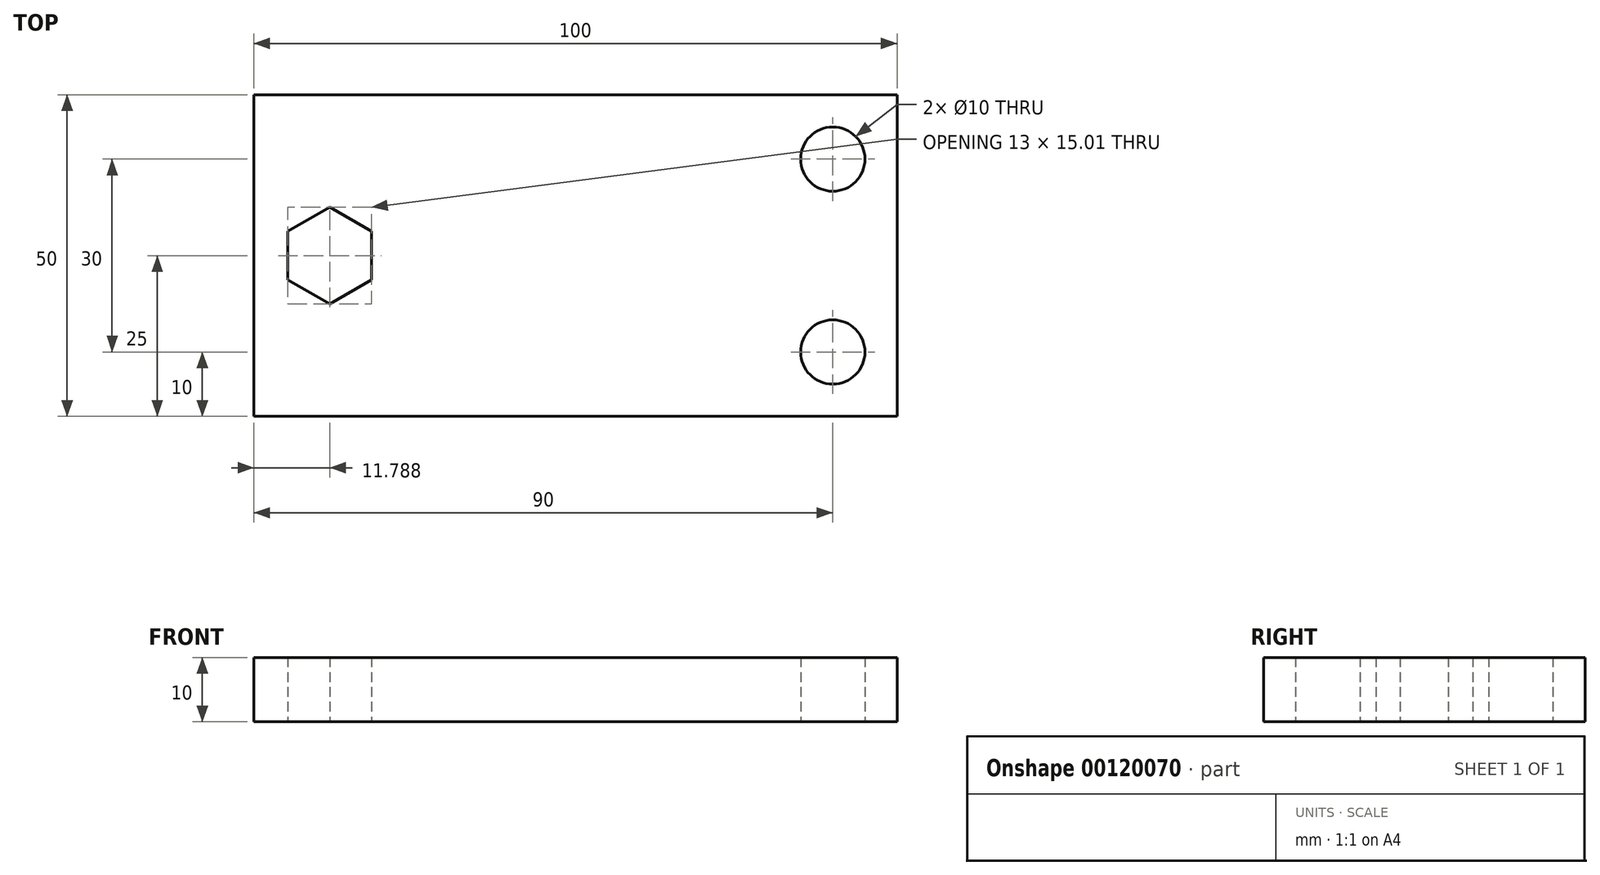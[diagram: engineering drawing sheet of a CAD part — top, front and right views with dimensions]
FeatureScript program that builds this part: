
annotation { "Feature Type Name" : "Feature", "Feature Type Description" : "" }
export const myFeature = defineFeature(function(context is Context, id is Id, definition is map)
    precondition{}
    {
        {
            var Q0;
            Q0=qCreatedBy(makeId("Top.planeOp"),FACE);
            var sketch = newSketch(context, id + "F0", { "sketchPlane" : qUnion([Q0])});
            skLineSegment(sketch, "E0.bottom", {"start": v(50, -25) * mm, "end": v(-50, -25) * mm});
            skLineSegment(sketch, "E0.top", {"start": v(50, 25) * mm, "end": v(-50, 25) * mm});
            skLineSegment(sketch, "E0.left", {"start": v(50, -25) * mm, "end": v(50, 25) * mm});
            skLineSegment(sketch, "E0.right", {"start": v(-50, -25) * mm, "end": v(-50, 25) * mm});
            skPoint(sketch, "E0.middle", {"position": v(0, 0) * mm});
            skCircle(sketch, "E1.cCircle", {"center": v(-38.21, 0) * mm, "radius": 6.5 * mm, "construction": true});
            skLineSegment(sketch, "E1.0", {"start": v(-31.71, -3.75) * mm, "end": v(-38.21, -7.5) * mm});
            skLineSegment(sketch, "E1.1", {"start": v(-38.21, -7.5) * mm, "end": v(-44.71, -3.75) * mm});
            skLineSegment(sketch, "E1.2", {"start": v(-44.71, -3.75) * mm, "end": v(-44.71, 3.75) * mm});
            skLineSegment(sketch, "E1.3", {"start": v(-44.71, 3.75) * mm, "end": v(-38.21, 7.5) * mm});
            skLineSegment(sketch, "E1.4", {"start": v(-38.21, 7.5) * mm, "end": v(-31.71, 3.75) * mm});
            skLineSegment(sketch, "E1.5", {"start": v(-31.71, 3.75) * mm, "end": v(-31.71, -3.75) * mm});
            skPoint(sketch, "E1.0.midPoint", {"position": v(-34.96, -5.63) * mm});
            skCircle(sketch, "E2", {"center": v(40, -15) * mm, "radius": 5 * mm});
            skCircle(sketch, "E3.MirrorC", {"center": v(40, 15) * mm, "radius": 5 * mm});
            skSolve(sketch);
        }
        {
            var Q0;
            Q0=makeQuery(id+"F0.imprint","IMPRINT",FACE,{"disambiguationData":[TD([[makeQuery(id+"F0.imprint","IMPRINT",EDGE,{"derivedFrom":sQuery(id+"F0.wireOp",EDGE,"E0.bottom")}),-1.0]])]});
            extrude(context, id + "F1", {"entities" : qUnion([Q0]), "depth" : 10 * mm});
        }
    });
